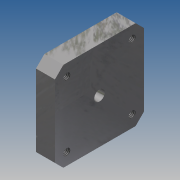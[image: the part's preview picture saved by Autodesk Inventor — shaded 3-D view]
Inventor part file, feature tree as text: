
AUTODESK INVENTOR PART (.ipt)
format: ipt  version: 2015 (Build 190159000, 159)  size: 162,304 bytes
history: native  units: mm
features: sketch x4, extrude x3, projected_geometry x3, hole x1
ambient origin geometry x8: Origin, YZ Plane, XZ Plane, XY Plane, X Axis, Y Axis, Z Axis, Center Point
bodies: Body1 (feature_tree)
feature tree (11):
  extrude  "Extrusion2"  Depth=42.3mm
  hole  "Bohrung1"  [1 undecoded]
  extrude  "Extrusion4"  Depth=4.0mm
  extrude  "Extrusion5"  Depth=3.0mm
  sketch  "Skizze1"  dims[d0=42.3mm d1=42.3mm]
  sketch  "Skizze2"  dims[d5=4.0mm d6=4.0mm]
  projected_geometry  "Projizierte Kontur1"
  sketch  "Skizze4"  dims[d7=4.0mm d8=4.0mm]
  projected_geometry  "Projizierte Kontur2"
  sketch  "Skizze5"  dims[d9=4.0mm d10=4.0mm d11=4.0mm d12=4.0mm d13=5.0mm d16=9.0mm d17=0.0mm d18=15.5mm d19=15.5mm d20=3.242mm d21=9.0mm d22=4.0mm d23=2.0mm d24=90.0deg d25=11.8mm d26=20.594885mm d34=7.0mm d35=7.0mm d36=7.0mm d37=7.0mm d38=3.0mm d39=0.0mm d40=7.0mm d41=3.0mm d42=0.0mm]
  projected_geometry  "Projizierte Kontur3"
note: 1 required parameter value undecoded (feature->parameter linkage not recoverable at this tier; creation-order binding heuristic only, values carry confidence <= 0.55)
